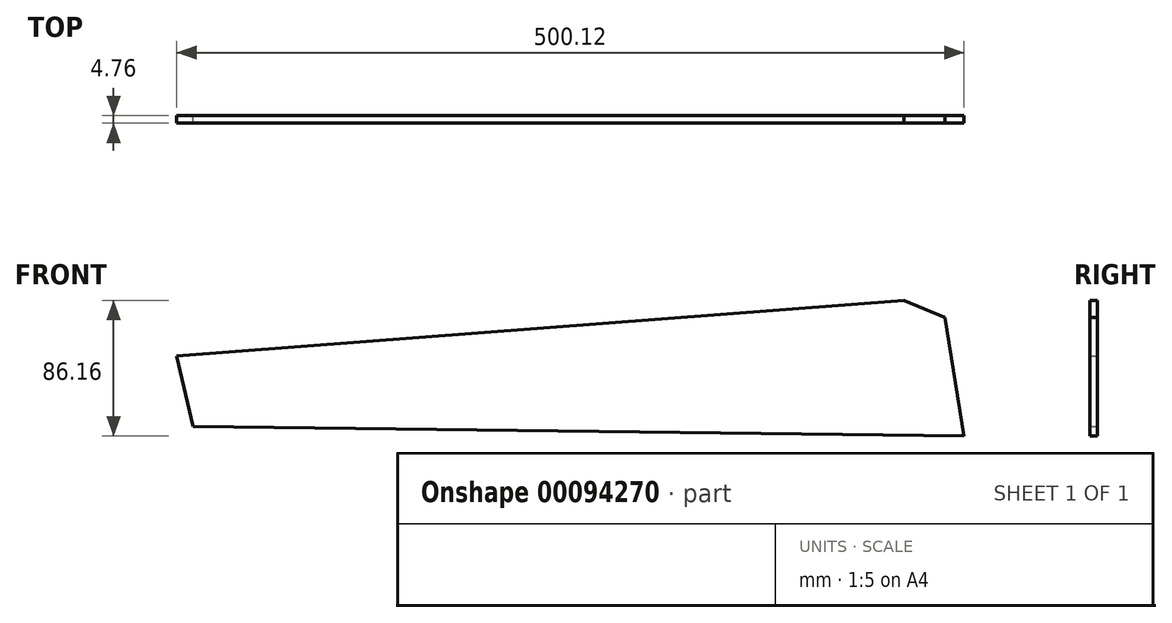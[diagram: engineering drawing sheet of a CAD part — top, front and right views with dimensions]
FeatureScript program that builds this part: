
annotation { "Feature Type Name" : "Feature", "Feature Type Description" : "" }
export const myFeature = defineFeature(function(context is Context, id is Id, definition is map)
    precondition{}
    {
        {
            var Q0;
            Q0=qCreatedBy(makeId("Front.planeOp"),FACE);
            var sketch = newSketch(context, id + "F0", { "sketchPlane" : qUnion([Q0])});
            skLineSegment(sketch, "E0", {"start": v(254.06, 0) * mm, "end": v(241.93, 75.23) * mm});
            skLineSegment(sketch, "E1", {"start": v(219.12, 86.4) * mm, "end": v(-262.07, 49.5) * mm});
            skLineSegment(sketch, "E2", {"start": v(241.93, 75.23) * mm, "end": v(215.95, 86.16) * mm});
            skLineSegment(sketch, "E3", {"start": v(254.06, 0) * mm, "end": v(-252.07, 6.19) * mm});
            skPoint(sketch, "E4.start.orphan", {"position": v(-250.64, 0) * mm});
            skLineSegment(sketch, "E5", {"start": v(-246.06, 50.73) * mm, "end": v(-235.73, 5.99) * mm});
            skSolve(sketch);
        }
        {
            var Q0;
            Q0 = qSketchRegion(id + "F0", true);
            extrude(context, id + "F1", {"entities" : qUnion([Q0]), "depth" : 4.76 * mm});
        }
    });
